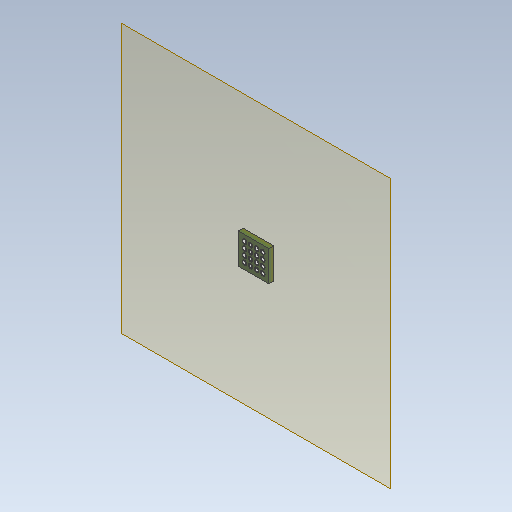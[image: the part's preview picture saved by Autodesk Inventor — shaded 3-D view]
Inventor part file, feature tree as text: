
AUTODESK INVENTOR PART (.ipt)
format: ipt  version: 2021 (Build 250183000, 183)  size: 208,896 bytes
history: native  units: in
note: dims shown in document units (in); Inventor stores cm internally (conversion verified against a paired STEP export)
features: other x3, sketch x3, plane x1
ambient origin geometry x8: Origin, YZ Plane, XZ Plane, XY Plane, X Axis, Y Axis, Z Axis, Center Point
bodies: Solid1 (feature_tree)
feature tree (7):
  other  "1.27mmpitchProtoboardDesign.ipt_.25inch_.25Inch.ipt"
  other  "Solid1::1.27mmpitchProtoboardDesign.ipt_.25inch_.25Inch.ipt"
  other  "TaggingFeature1"
  sketch  "Sketch1"  dims[d0=0.3937in]
  sketch  "Sketch2"  dims[d1=0.12in]
  sketch  "Sketch3"
  plane  "Work Plane1"
